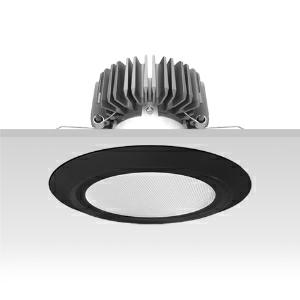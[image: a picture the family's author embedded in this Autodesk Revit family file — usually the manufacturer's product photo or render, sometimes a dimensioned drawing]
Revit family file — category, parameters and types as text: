
# Revit family: 3f_filippi_-_3f_reno_bianco_ampio_3f_filippi_-_30633_a01049_-_3f_reno_200_wh_3000-930_wide___smp_bk_7469
name_source: partatom
category: Lighting Fixtures
units: mm (PartAtom-declared; Revit-internal decimal feet)

## family parameters
Cut with Voids When Loaded = No
Host = Face
Light Source = No
Part Type = Normal
Room Calculation Point = No
Round Connector Dimension = Use Diameter
Shared = No

## types (1)
- 3F Filippi - 3F Reno Bianco Ampio (1 x LED, 2320 lm, 37 W, 3000 K)
    Apparent Load = 37 VA
    Approval mark = CE
    CIE Flux Codes = 74 92 98 100 100
    Color Rendering = 90
    Color Temperature = 3000 K
    Control Gear = Electronic ballast
    Default Elevation = 1800 mm
    Description = ILLUMINOTECHNICAL
Luminous efficiency 100% (DLOR 100%, ULOR 0%).
Initial luminous flux of the luminaire 2320 lm.
Direct symmetric wide distribution.
Installation Interdistance Transv.D = 1.06 x hu - Long.D = 1.04 x hu.
Tabular UGR (CIE 117 - 4H-8H; S=0.25H; 70/50/20): RUG 22.5 - 22.3.
Beam angle: 70° - 69°.
Luminous efficacy 63 lm/W.
Lifetime (L90/B10): 30000 h. (tq+25°C)
Lifetime (L85/B10): 50000 h. (tq+25°C)
Lifetime (L70/B10): 80000 h. (tq+25°C)
Sudden decreased luminous flux after 50000 hours: 0% (C0).
Photobiological safety in compliance with IEC/TR 62778: RG0 risk exempt, (IEC 62471).
In compliance with IEC/EN 62722-2-1 - IEC/EN 62717 standards.

SOURCE
Compact LED module 3000/930.
Energy efficiency class (UE 2019/2020 - UE 2019/2015): E.
CIE 13.3 Colour rendering index: CRI >90 (R9 >50%).
IES TM-30 Fidelity Index: Rf = 92 Rg = 101.
CCT nominal colour temperature 3000 K.
Colour initial tolerance (MacAdam): SDCM 3.
Zhaga Book 3 compliant.

MECHANICAL
Passive heat dissipator in die-casting aluminium, oversized, for optimum thermal management of the LED module.
Parabolic element with graduated/concentric rings in white polycarbonate.
Transparent external lens with glossy and satin differentiated surfaces, with a cooling and anti-insect system in methacrylate (PMMA).
Fastening spring clips in stainless steel.
Dimensions: diameter 226 mm, height 146 mm. Weight 1.645 kg.
IP44 protection degree for exposed part, IP20 for recessed part.
Mechanical strength to impacts IK05 (0.7 joule).
Glow-wire test resistance 650°C.

ELECTRICAL
Wiring on a separate unit.
Halogen Free electronic wiring 230V-50/60Hz, power factor 0.95, THD <25%, constant output current, SELV, class II, 1 driver.
Power of the luminaire 37 W.
ENEC - CE.
SAFE FLICKER: PstLM=<1 and SVM=<0.4 (IEC TR 61547-1 and IEC TR 63158), to ensure a more comfortable and safe light.
Luminaire compliant with EN 60598-2-22 for power supply from a centralised emergency system CPSS (Central Power Supply System), not incorporated in the luminaire - high risk areas excluded. The default power and flux are 100% in AC and 100% in DC.
Ambient temperature from 0°C to +25°C.
Temperature class T6 max 85°C.
Relative humidity UR: <85%.

INSTALLATION
Pull-up recessed fitting.
False ceiling carving: 200 mm.
All accessories dedicated to this product are available on the Catalog and on our website www.3F-Filippi.com.

ACCESSORIES
A01049 - Anti-glare microprismatic SMP diffuser in methacrylate (PMMA), locked and in line with the trim, in black polycarbonate.

APPLICATIONS
Suitable product for food production plants (HACCP), IFS (Food Version 6), BRC (GSFS Food Version 7).
Environments: architectural, commercial, exhibition areas, transit areas, corridors, shops, display windows, service areas.
In false ceilings with narrow voids.

WARNING
Luminaire designed for disposal/recycling at end-of-life.
Replaceable (LED only) light source by a professional. Replaceable control gear by a professional.
    Height = 0 mm  [stored 0 ft]
    Lamp = 1 x LED
    Lamp Light Flux = 2320 lm
    Lamp Power = 37 W
    Lamp count = 1
    Length = 226 mm
    Lifetime = 50000 h
    Luminous efficacy = 63 lm/W
    Manufacturer = 3F Filippi
    ModVariant = No
    Model = 3F Filippi - 30633+A01049 - 3F Reno 200 WH 3000-930 WIDE + SMP BK
    Mounting Place = Ceiling
    Mounting Type = Recessed
    Number of Poles = 1
    OnlyDefault = Yes
    Power Factor = 1
    Product Name = 3F Filippi - 3F Reno Bianco Ampio
    Product group = recessed luminaire
    ProductGroupID = 4
    Protection Class = Protection class II
    Protection Degree = IP 20
    RLX_Detail_Level = 1
    RLX_Emergency_Light_Flux = 0 lm
    RLX_Emergency_Type = 0
    RLX_Emergency_Type_DB = No
    RlxData = <blob elided: 97553 chars, md5=f458d1e1>
    Socket = socket
    Standby Power = 0 W
    System Light Flux = 2320 lm
    System Power = 37 W
    Type Comments = Product without accessories
    Type Image = 3ffilippi_3f_reno_200_bk_vs_smp.jpg
    URL = http://relux.com
    VarID = ---
    Voltage = 0 V
    Weight = 0.00 kg
    Width = 0 mm  [stored 0 ft]

note: [stored X ft] marks values corroborated as IEEE doubles in the binary element streams (Revit-internal decimal feet)

## geometry (parser evidence)
native form markers: Blend x4, Sweep x11
no freeform markers — native parametric forms only
